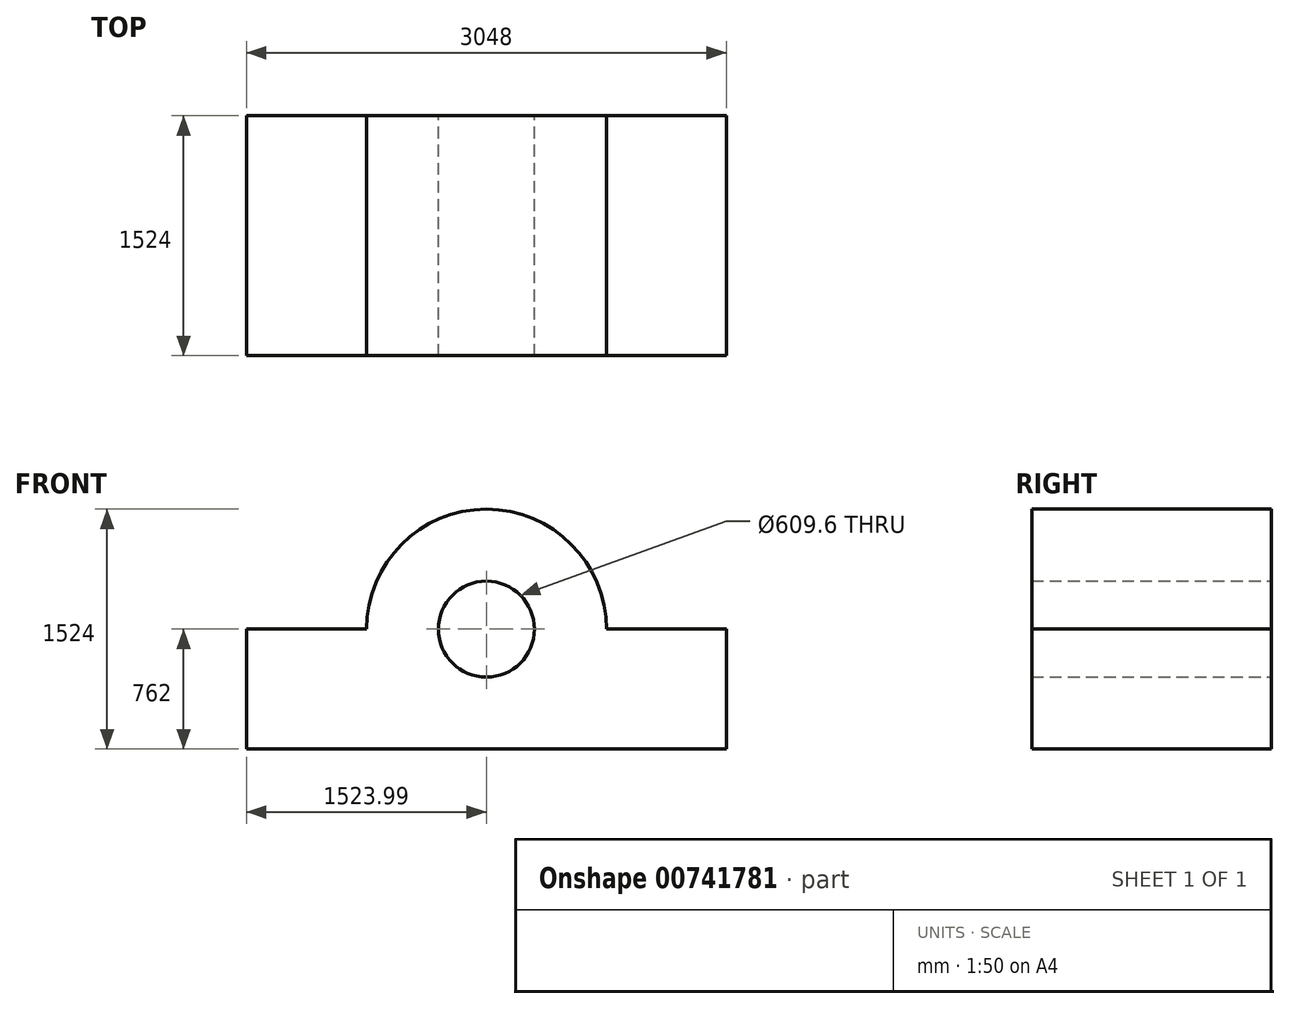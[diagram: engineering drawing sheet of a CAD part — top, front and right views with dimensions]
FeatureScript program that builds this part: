
annotation { "Feature Type Name" : "Feature", "Feature Type Description" : "" }
export const myFeature = defineFeature(function(context is Context, id is Id, definition is map)
    precondition{}
    {
        {
            var Q0;
            Q0=qCreatedBy(makeId("Front.planeOp"),FACE);
            var sketch = newSketch(context, id + "F0", { "sketchPlane" : qUnion([Q0])});
            skLineSegment(sketch, "E0", {"start": v(-441.34, 0) * mm, "end": v(2606.66, 0) * mm});
            skLineSegment(sketch, "E1", {"start": v(2606.66, 0) * mm, "end": v(2606.66, 762) * mm});
            skLineSegment(sketch, "E2", {"start": v(2606.66, 762) * mm, "end": v(1844.66, 762) * mm});
            skLineSegment(sketch, "E3", {"start": v(-441.34, 762) * mm, "end": v(-441.34, 0) * mm});
            skCircle(sketch, "E4", {"center": v(1082.66, 762) * mm, "radius": 304.8 * mm});
            skArc(sketch, "E5", {"start": v(1844.66, 762) * mm, "mid": v(1082.66, 1524) * mm, "end": v(320.66, 762) * mm});
            skLineSegment(sketch, "E6.trimOffspring", {"start": v(320.66, 762) * mm, "end": v(-441.34, 762) * mm});
            skSolve(sketch);
        }
        {
            var Q0;
            Q0 = qSketchRegion(id + "F0", true);
            extrude(context, id + "F1", {"entities" : qUnion([Q0]), "depth" : 1524 * mm, "offsetDistance" : 25.4 * mm});
        }
    });
